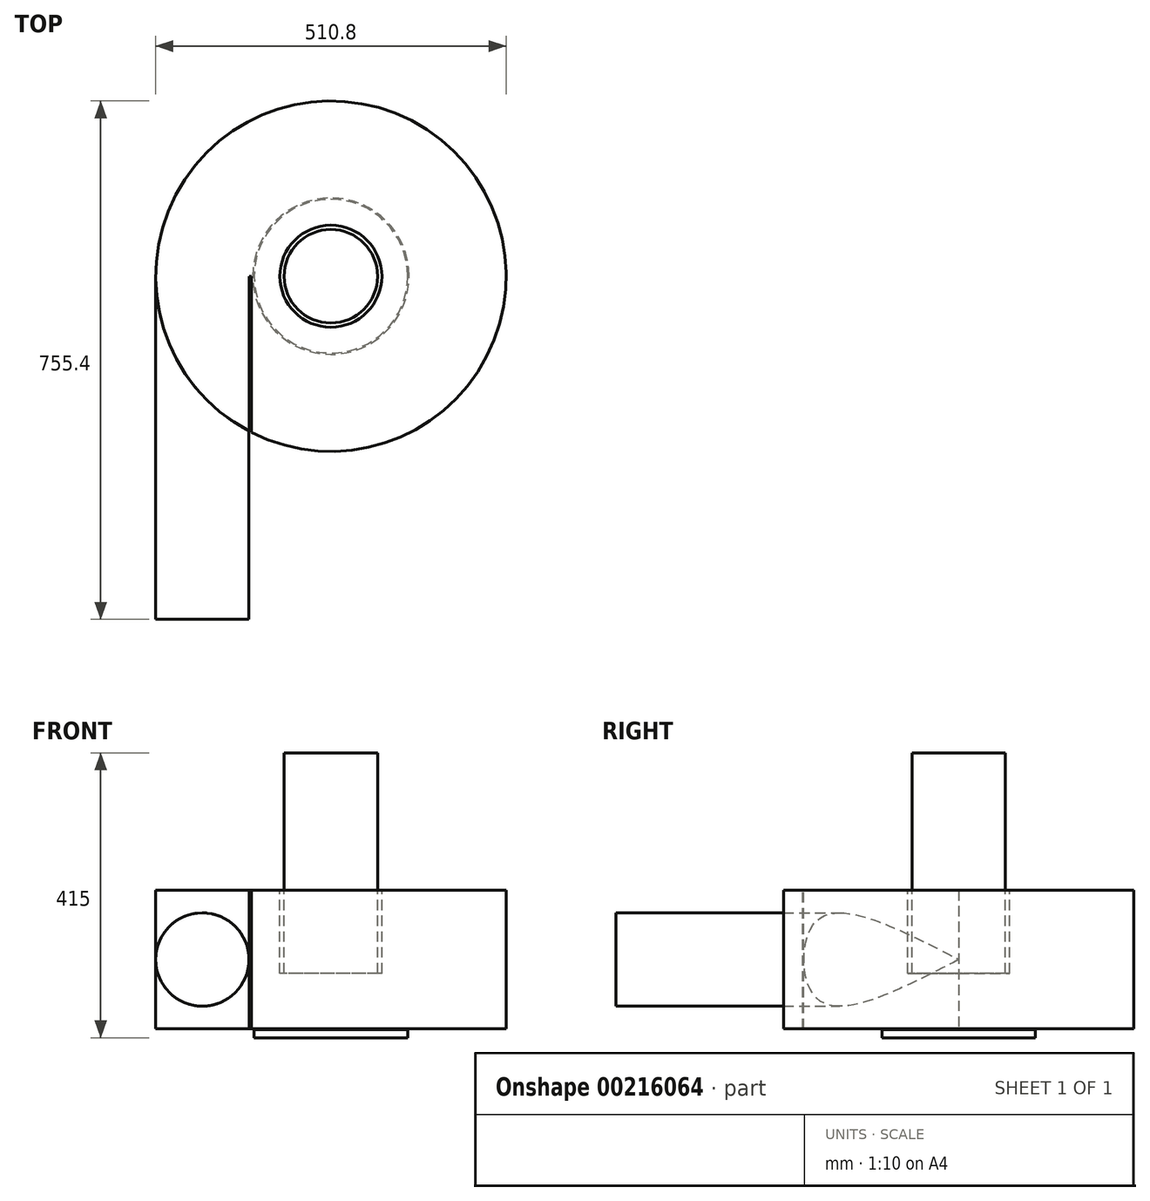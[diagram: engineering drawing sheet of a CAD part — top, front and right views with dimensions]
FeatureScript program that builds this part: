
annotation { "Feature Type Name" : "Feature", "Feature Type Description" : "" }
export const myFeature = defineFeature(function(context is Context, id is Id, definition is map)
    precondition{}
    {
        {
            var Q0;
            Q0=qCreatedBy(makeId("Front.planeOp"),FACE);
            var sketch = newSketch(context, id + "F0", { "sketchPlane" : qUnion([Q0])});
            skLineSegment(sketch, "E0", {"start": v(-114, 169) * mm, "end": v(-255.4, 169) * mm});
            skLineSegment(sketch, "E1", {"start": v(-255.4, 169) * mm, "end": v(-255.4, 371) * mm});
            skLineSegment(sketch, "E2", {"start": v(-255.4, 371) * mm, "end": v(-74.4, 371) * mm});
            skLineSegment(sketch, "E3", {"start": v(-74.4, 371) * mm, "end": v(-74.4, 250) * mm});
            skLineSegment(sketch, "E4", {"start": v(-74.4, 250) * mm, "end": v(-68.2, 250) * mm});
            skLineSegment(sketch, "E5", {"start": v(-68.2, 250) * mm, "end": v(-68.2, 371) * mm});
            skLineSegment(sketch, "E6", {"start": v(-68.2, 371) * mm, "end": v(0, 371) * mm});
            skLineSegment(sketch, "E7", {"start": v(-114, 169) * mm, "end": v(-112, 168) * mm});
            skLineSegment(sketch, "E8", {"start": v(-112, 168) * mm, "end": v(-112, 156) * mm});
            skLineSegment(sketch, "E9", {"start": v(-112, 156) * mm, "end": v(0, 156) * mm});
            skLineSegment(sketch, "E10", {"start": v(0, 371) * mm, "end": v(0, 156) * mm});
            skSolve(sketch);
        }
        {
            var Q0;
            Q0=makeQuery(id+"F0.imprint","IMPRINT",FACE,{"disambiguationData":[TD([[makeQuery(id+"F0.imprint","IMPRINT",EDGE,{"derivedFrom":sQuery(id+"F0.wireOp",EDGE,"E0")}),-1.0]])]});
            var Q1;
            Q1=sQuery(id+"F0.wireOp",EDGE,"E10");
            revolve(context, id + "F1", {"entities" : qUnion([Q0]), "axis" : qUnion([Q1]), "revolveType" : RevolveType.FULL});
        }
        {
            var Q0;
            Q0=qCreatedBy(makeId("Front.planeOp"),FACE);
            var sketch = newSketch(context, id + "F2", { "sketchPlane" : qUnion([Q0])});
            skCircle(sketch, "E11", {"center": v(-187.4, 270) * mm, "radius": 68 * mm});
            skSolve(sketch);
        }
        {
            var Q0;
            Q0=qSketchRegion(id+"F2",true);
            extrude(context, id + "F3", {"entities" : qUnion([Q0]), "operationType" : NewBodyOperationType.ADD, "depth" : 500 * mm});
        }
        {
            var Q0;
            Q0=makeQuery(id+"F1.opRevolve","SWEPT_FACE",FACE,{"disambiguationData":[OSD([sQuery(id+"F0.wireOp",EDGE,"E6")])]});
            extrude(context, id + "F4", {"entities" : qUnion([Q0]), "operationType" : NewBodyOperationType.ADD, "depth" : 200 * mm});
        }
        {
            var Q0;
            Q0=qCreatedBy(makeId("Top.planeOp"),FACE);
            var sketch = newSketch(context, id + "F5", { "sketchPlane" : qUnion([Q0])});
            skLineSegment(sketch, "E12.bottom", {"start": v(-119, -250) * mm, "end": v(-116, -250) * mm});
            skLineSegment(sketch, "E12.top", {"start": v(-119, 0) * mm, "end": v(-116, 0) * mm});
            skLineSegment(sketch, "E12.left", {"start": v(-119, 0) * mm, "end": v(-119, -250) * mm});
            skLineSegment(sketch, "E12.right", {"start": v(-116, 0) * mm, "end": v(-116, -250) * mm});
            skSolve(sketch);
        }
        {
            var Q0;
            Q0 = qSketchRegion(id + "F5", true);
            extrude(context, id + "F6", {"entities" : qUnion([Q0]), "operationType" : NewBodyOperationType.REMOVE, "depth" : 375 * mm});
        }
    });
